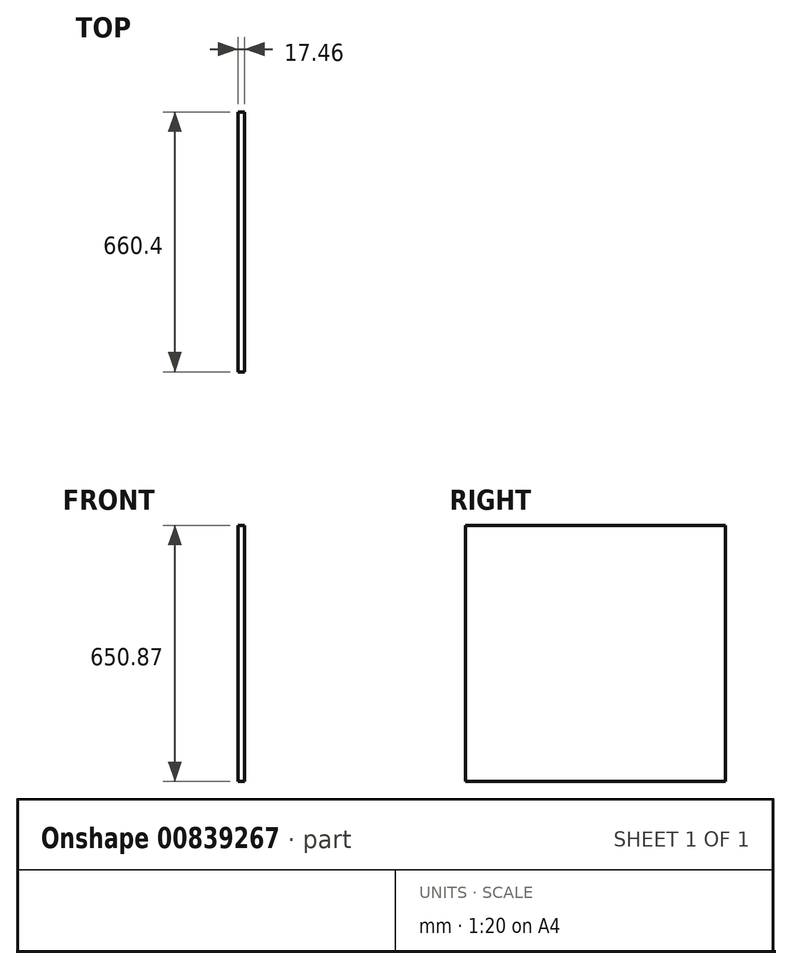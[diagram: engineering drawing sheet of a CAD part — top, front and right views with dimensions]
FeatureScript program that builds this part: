
annotation { "Feature Type Name" : "Feature", "Feature Type Description" : "" }
export const myFeature = defineFeature(function(context is Context, id is Id, definition is map)
    precondition{}
    {
        {
            var Q0;
            Q0=qCreatedBy(makeId("Right.planeOp"),FACE);
            var sketch = newSketch(context, id + "F0", { "sketchPlane" : qUnion([Q0])});
            skLineSegment(sketch, "E0.bottom", {"start": v(-405.46, 405.74) * mm, "end": v(254.94, 405.74) * mm});
            skLineSegment(sketch, "E0.top", {"start": v(-405.46, -245.13) * mm, "end": v(254.94, -245.13) * mm});
            skLineSegment(sketch, "E0.left", {"start": v(-405.46, 405.74) * mm, "end": v(-405.46, -245.13) * mm});
            skLineSegment(sketch, "E0.right", {"start": v(254.94, 405.74) * mm, "end": v(254.94, -245.13) * mm});
            skSolve(sketch);
        }
        {
            var Q0;
            Q0=makeQuery(id+"F0.imprint","IMPRINT",FACE,{"disambiguationData":[TD([[makeQuery(id+"F0.imprint","IMPRINT",EDGE,{"derivedFrom":sQuery(id+"F0.wireOp",EDGE,"E0.bottom")}),-1.0]])]});
            extrude(context, id + "F1", {"entities" : qUnion([Q0]), "depth" : 17.46 * mm, "offsetDistance" : 25.4 * mm});
        }
    });
